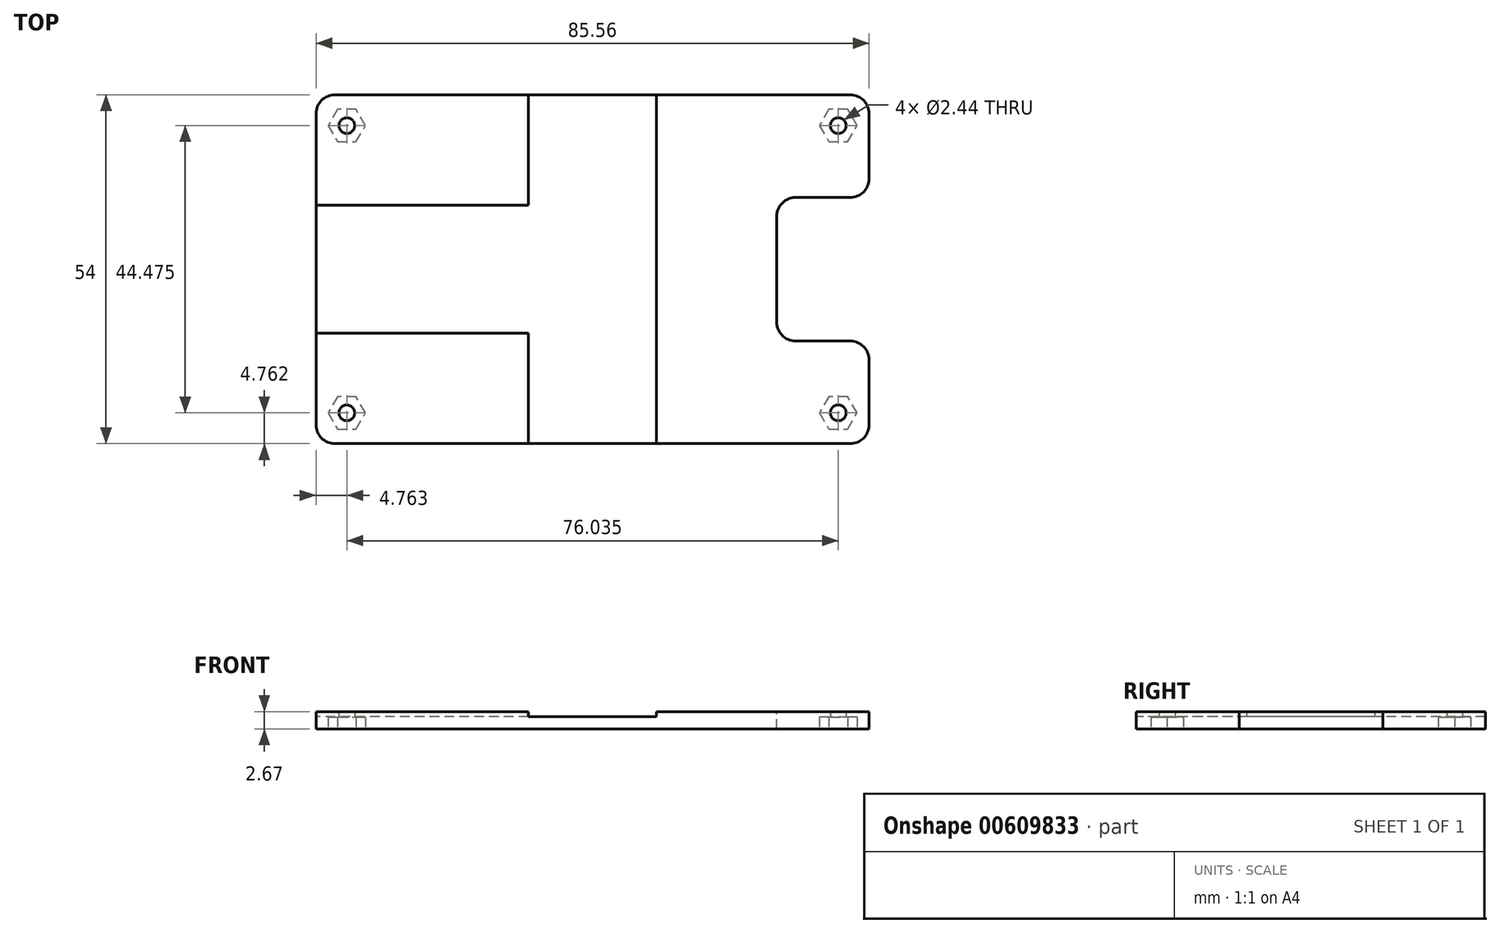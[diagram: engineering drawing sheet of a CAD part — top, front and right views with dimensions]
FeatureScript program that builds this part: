
annotation { "Feature Type Name" : "Feature", "Feature Type Description" : "" }
export const myFeature = defineFeature(function(context is Context, id is Id, definition is map)
    precondition{}
    {
        {
            var Q0;
            Q0=qCreatedBy(makeId("Top.planeOp"),FACE);
            var sketch = newSketch(context, id + "F0", { "sketchPlane" : qUnion([Q0])});
            skLineSegment(sketch, "E0.bottom", {"start": v(-39.86, 27) * mm, "end": v(39.86, 27) * mm});
            skLineSegment(sketch, "E0.top", {"start": v(-39.86, -27) * mm, "end": v(39.86, -27) * mm});
            skLineSegment(sketch, "E0.left", {"start": v(-42.78, 24.08) * mm, "end": v(-42.78, -24.08) * mm});
            skLineSegment(sketch, "E0.right", {"start": v(42.78, 24.08) * mm, "end": v(42.78, -24.08) * mm});
            skPoint(sketch, "E0.middle", {"position": v(0, 0) * mm});
            skPoint(sketch, "E1.visualSharp", {"position": v(-42.78, 27) * mm});
            skArc(sketch, "E1.filletArc", {"start": v(-39.86, 27) * mm, "mid": v(-41.92, 26.14) * mm, "end": v(-42.78, 24.08) * mm});
            skPoint(sketch, "E2.visualSharp", {"position": v(-42.78, -27) * mm});
            skArc(sketch, "E2.filletArc", {"start": v(-42.78, -24.08) * mm, "mid": v(-41.92, -26.14) * mm, "end": v(-39.86, -27) * mm});
            skPoint(sketch, "E3.visualSharp", {"position": v(42.78, -27) * mm});
            skArc(sketch, "E3.filletArc", {"start": v(39.86, -27) * mm, "mid": v(41.92, -26.14) * mm, "end": v(42.78, -24.08) * mm});
            skPoint(sketch, "E4.visualSharp", {"position": v(42.78, 27) * mm});
            skArc(sketch, "E4.filletArc", {"start": v(42.78, 24.08) * mm, "mid": v(41.92, 26.14) * mm, "end": v(39.86, 27) * mm});
            skSolve(sketch);
        }
        {
            var Q0;
            Q0 = qSketchRegion(id + "F0", true);
            extrude(context, id + "F1", {"entities" : qUnion([Q0]), "depth" : 2.67 * mm, "offsetDistance" : 25.4 * mm});
        }
        {
            var Q0;
            Q0=makeQuery(id+"F1.opExtrude","CAP_FACE",FACE,{"disambiguationData":[OSD([sQuery(id+"F0.wireOp",EDGE,"E0.bottom"),sQuery(id+"F0.wireOp",EDGE,"E0.top"),sQuery(id+"F0.wireOp",EDGE,"E0.left"),sQuery(id+"F0.wireOp",EDGE,"E0.right"),sQuery(id+"F0.wireOp",EDGE,"E1.filletArc"),sQuery(id+"F0.wireOp",EDGE,"E2.filletArc"),sQuery(id+"F0.wireOp",EDGE,"E3.filletArc"),sQuery(id+"F0.wireOp",EDGE,"E4.filletArc")])],"isStart":true});
            var sketch = newSketch(context, id + "F2", { "sketchPlane" : qUnion([Q0])});
            skLineSegment(sketch, "E5.bottom", {"start": v(-38.02, 22.24) * mm, "end": v(38.02, 22.24) * mm, "construction": true});
            skLineSegment(sketch, "E5.top", {"start": v(-38.02, -22.24) * mm, "end": v(38.02, -22.24) * mm, "construction": true});
            skLineSegment(sketch, "E5.left", {"start": v(-38.02, 22.24) * mm, "end": v(-38.02, -22.24) * mm, "construction": true});
            skLineSegment(sketch, "E5.right", {"start": v(38.02, 22.24) * mm, "end": v(38.02, -22.24) * mm, "construction": true});
            skPoint(sketch, "E5.middle", {"position": v(0, 0) * mm});
            skLineSegment(sketch, "E6", {"start": v(0, 22.24) * mm, "end": v(0, 27) * mm, "construction": true});
            skLineSegment(sketch, "E7", {"start": v(-38.02, 0) * mm, "end": v(-42.78, 0) * mm, "construction": true});
            skCircle(sketch, "E8", {"center": v(-38.02, 22.24) * mm, "radius": 1.22 * mm});
            skCircle(sketch, "E9", {"center": v(-38.02, -22.24) * mm, "radius": 1.22 * mm});
            skCircle(sketch, "E10", {"center": v(38.02, -22.24) * mm, "radius": 1.22 * mm});
            skCircle(sketch, "E11", {"center": v(38.02, 22.24) * mm, "radius": 1.22 * mm});
            skSolve(sketch);
        }
        {
            var Q0;
            Q0 = qSketchRegion(id + "F2", true);
            extrude(context, id + "F3", {"entities" : qUnion([Q0]), "operationType" : NewBodyOperationType.REMOVE, "endBound" : BoundingType.THROUGH_ALL, "oppositeDirection" : true, "depth" : 25.4 * mm, "offsetDistance" : 25.4 * mm});
        }
        {
            var Q0;
            Q0=makeQuery(id+"F1.opExtrude","CAP_FACE",FACE,{"disambiguationData":[OSD([sQuery(id+"F0.wireOp",EDGE,"E0.bottom"),sQuery(id+"F0.wireOp",EDGE,"E0.top"),sQuery(id+"F0.wireOp",EDGE,"E0.left"),sQuery(id+"F0.wireOp",EDGE,"E0.right"),sQuery(id+"F0.wireOp",EDGE,"E1.filletArc"),sQuery(id+"F0.wireOp",EDGE,"E2.filletArc"),sQuery(id+"F0.wireOp",EDGE,"E3.filletArc"),sQuery(id+"F0.wireOp",EDGE,"E4.filletArc")])],"isStart":true});
            var sketch = newSketch(context, id + "F4", { "sketchPlane" : qUnion([Q0])});
            skCircle(sketch, "E12.cCircle", {"center": v(-38.02, 22.24) * mm, "radius": 2.5 * mm, "construction": true});
            skLineSegment(sketch, "E12.0", {"start": v(-35.12, 22.24) * mm, "end": v(-36.57, 19.73) * mm});
            skLineSegment(sketch, "E12.1", {"start": v(-36.57, 19.73) * mm, "end": v(-39.47, 19.73) * mm});
            skLineSegment(sketch, "E12.2", {"start": v(-39.47, 19.73) * mm, "end": v(-40.91, 22.24) * mm});
            skLineSegment(sketch, "E12.3", {"start": v(-40.91, 22.24) * mm, "end": v(-39.47, 24.75) * mm});
            skLineSegment(sketch, "E12.4", {"start": v(-39.47, 24.75) * mm, "end": v(-36.57, 24.75) * mm});
            skLineSegment(sketch, "E12.5", {"start": v(-36.57, 24.75) * mm, "end": v(-35.12, 22.24) * mm});
            skPoint(sketch, "E12.0.midPoint", {"position": v(-35.85, 20.98) * mm});
            skCircle(sketch, "E13.cCircle", {"center": v(-38.02, -22.24) * mm, "radius": 2.5 * mm, "construction": true});
            skLineSegment(sketch, "E13.0", {"start": v(-36.57, -19.73) * mm, "end": v(-35.12, -22.24) * mm});
            skLineSegment(sketch, "E13.1", {"start": v(-35.12, -22.24) * mm, "end": v(-36.57, -24.75) * mm});
            skLineSegment(sketch, "E13.2", {"start": v(-36.57, -24.75) * mm, "end": v(-39.47, -24.75) * mm});
            skLineSegment(sketch, "E13.3", {"start": v(-39.47, -24.75) * mm, "end": v(-40.91, -22.24) * mm});
            skLineSegment(sketch, "E13.4", {"start": v(-40.91, -22.24) * mm, "end": v(-39.47, -19.73) * mm});
            skLineSegment(sketch, "E13.5", {"start": v(-39.47, -19.73) * mm, "end": v(-36.57, -19.73) * mm});
            skPoint(sketch, "E13.0.midPoint", {"position": v(-35.85, -20.98) * mm});
            skCircle(sketch, "E14.cCircle", {"center": v(38.02, 22.24) * mm, "radius": 2.5 * mm, "construction": true});
            skLineSegment(sketch, "E14.0", {"start": v(36.57, 19.73) * mm, "end": v(35.12, 22.24) * mm});
            skLineSegment(sketch, "E14.1", {"start": v(35.12, 22.24) * mm, "end": v(36.57, 24.75) * mm});
            skLineSegment(sketch, "E14.2", {"start": v(36.57, 24.75) * mm, "end": v(39.47, 24.75) * mm});
            skLineSegment(sketch, "E14.3", {"start": v(39.47, 24.75) * mm, "end": v(40.91, 22.24) * mm});
            skLineSegment(sketch, "E14.4", {"start": v(40.91, 22.24) * mm, "end": v(39.47, 19.73) * mm});
            skLineSegment(sketch, "E14.5", {"start": v(39.47, 19.73) * mm, "end": v(36.57, 19.73) * mm});
            skPoint(sketch, "E14.0.midPoint", {"position": v(35.85, 20.98) * mm});
            skCircle(sketch, "E15.cCircle", {"center": v(38.02, -22.24) * mm, "radius": 2.5 * mm, "construction": true});
            skLineSegment(sketch, "E15.0", {"start": v(35.12, -22.24) * mm, "end": v(36.57, -19.73) * mm});
            skLineSegment(sketch, "E15.1", {"start": v(36.57, -19.73) * mm, "end": v(39.47, -19.73) * mm});
            skLineSegment(sketch, "E15.2", {"start": v(39.47, -19.73) * mm, "end": v(40.91, -22.24) * mm});
            skLineSegment(sketch, "E15.3", {"start": v(40.91, -22.24) * mm, "end": v(39.47, -24.75) * mm});
            skLineSegment(sketch, "E15.4", {"start": v(39.47, -24.75) * mm, "end": v(36.57, -24.75) * mm});
            skLineSegment(sketch, "E15.5", {"start": v(36.57, -24.75) * mm, "end": v(35.12, -22.24) * mm});
            skPoint(sketch, "E15.0.midPoint", {"position": v(35.85, -20.98) * mm});
            skSolve(sketch);
        }
        {
            var Q0;
            Q0 = qSketchRegion(id + "F4", true);
            extrude(context, id + "F5", {"entities" : qUnion([Q0]), "operationType" : NewBodyOperationType.REMOVE, "oppositeDirection" : true, "depth" : 1.84 * mm, "offsetDistance" : 25.4 * mm});
        }
        {
            var Q0;
            Q0=makeQuery(id+"F1.opExtrude","CAP_FACE",FACE,{"disambiguationData":[OSD([sQuery(id+"F0.wireOp",EDGE,"E0.bottom"),sQuery(id+"F0.wireOp",EDGE,"E0.top"),sQuery(id+"F0.wireOp",EDGE,"E0.left"),sQuery(id+"F0.wireOp",EDGE,"E0.right"),sQuery(id+"F0.wireOp",EDGE,"E1.filletArc"),sQuery(id+"F0.wireOp",EDGE,"E2.filletArc"),sQuery(id+"F0.wireOp",EDGE,"E3.filletArc"),sQuery(id+"F0.wireOp",EDGE,"E4.filletArc")])],"isStart":false});
            var sketch = newSketch(context, id + "F6", { "sketchPlane" : qUnion([Q0])});
            skLineSegment(sketch, "E16", {"start": v(0, 27) * mm, "end": v(0, -27) * mm, "construction": true});
            skLineSegment(sketch, "E17", {"start": v(0, 0) * mm, "end": v(-42.78, 0) * mm, "construction": true});
            skLineSegment(sketch, "E18.0", {"start": v(-9.9, 27) * mm, "end": v(-9.9, 9.9) * mm});
            skLineSegment(sketch, "E19.0", {"start": v(9.9, 27) * mm, "end": v(9.9, -27) * mm});
            skLineSegment(sketch, "E20", {"start": v(-9.9, 27) * mm, "end": v(9.9, 27) * mm});
            skLineSegment(sketch, "E21", {"start": v(-9.9, -27) * mm, "end": v(9.9, -27) * mm});
            skLineSegment(sketch, "E22.0", {"start": v(-9.9, 9.9) * mm, "end": v(-42.78, 9.9) * mm});
            skLineSegment(sketch, "E23.0", {"start": v(-9.9, -9.9) * mm, "end": v(-42.78, -9.9) * mm});
            skLineSegment(sketch, "E24", {"start": v(-42.78, 9.9) * mm, "end": v(-42.78, -9.9) * mm});
            skLineSegment(sketch, "E25.trimOffspring", {"start": v(-9.9, -9.9) * mm, "end": v(-9.9, -27) * mm});
            skSolve(sketch);
        }
        {
            var Q0;
            Q0 = qSketchRegion(id + "F6", true);
            extrude(context, id + "F7", {"entities" : qUnion([Q0]), "operationType" : NewBodyOperationType.REMOVE, "oppositeDirection" : true, "depth" : 0.76 * mm, "offsetDistance" : 25.4 * mm});
        }
        {
            var Q0;
            {var subQ0=sQuery(id+"F0.wireOp",EDGE,"E3.filletArc");var subQ1=sQuery(id+"F0.wireOp",EDGE,"E0.top");var subQ2=sQuery(id+"F0.wireOp",EDGE,"E0.right");var subQ3=sQuery(id+"F0.wireOp",EDGE,"E0.bottom");var subQ4=sQuery(id+"F0.wireOp",EDGE,"E4.filletArc");Q0=makeQuery(id+"F7.boolean.opBoolean","SPLIT",FACE,{"disambiguationData":[TD([makeQuery(id+"F1.opExtrude","SWEPT_FACE",FACE,{"disambiguationData":[OSD([subQ2])]})])],"derivedFrom":makeQuery(id+"F1.opExtrude","CAP_FACE",FACE,{"disambiguationData":[OSD([subQ3,subQ1,sQuery(id+"F0.wireOp",EDGE,"E0.left"),subQ2,sQuery(id+"F0.wireOp",EDGE,"E1.filletArc"),sQuery(id+"F0.wireOp",EDGE,"E2.filletArc"),subQ0,subQ4])],"isStart":false})});}
            var sketch = newSketch(context, id + "F8", { "sketchPlane" : qUnion([Q0])});
            skLineSegment(sketch, "E26.bottom", {"start": v(31.41, 11.11) * mm, "end": v(57.07, 11.11) * mm});
            skLineSegment(sketch, "E26.top", {"start": v(31.41, -11.11) * mm, "end": v(57.07, -11.11) * mm});
            skLineSegment(sketch, "E26.left", {"start": v(28.5, 8.2) * mm, "end": v(28.5, -8.2) * mm});
            skLineSegment(sketch, "E26.right", {"start": v(57.07, 11.11) * mm, "end": v(57.07, -11.11) * mm});
            skPoint(sketch, "E26.middle", {"position": v(42.78, 0) * mm});
            skPoint(sketch, "E27.visualSharp", {"position": v(28.5, 11.11) * mm});
            skArc(sketch, "E27.filletArc", {"start": v(31.41, 11.11) * mm, "mid": v(29.35, 10.26) * mm, "end": v(28.5, 8.2) * mm});
            skPoint(sketch, "E28.visualSharp", {"position": v(28.5, -11.11) * mm});
            skArc(sketch, "E28.filletArc", {"start": v(28.5, -8.2) * mm, "mid": v(29.35, -10.26) * mm, "end": v(31.41, -11.11) * mm});
            skSolve(sketch);
        }
        {
            var Q0;
            Q0 = qSketchRegion(id + "F8", true);
            extrude(context, id + "F9", {"entities" : qUnion([Q0]), "operationType" : NewBodyOperationType.REMOVE, "endBound" : BoundingType.THROUGH_ALL, "oppositeDirection" : true, "depth" : 25.4 * mm, "offsetDistance" : 25.4 * mm});
        }
        {
            var Q0;
            Q0=makeQuery(id+"F9.boolean.opBoolean","INTERSECT",EDGE,{"derivedFrom":[makeQuery(id+"F1.opExtrude","SWEPT_FACE",FACE,{"disambiguationData":[OSD([sQuery(id+"F0.wireOp",EDGE,"E0.right")])]}),makeQuery(id+"F9.opExtrude","SWEPT_FACE",FACE,{"disambiguationData":[OSD([sQuery(id+"F8.wireOp",EDGE,"E26.bottom")])]})]});
            var Q1;
            Q1=makeQuery(id+"F9.boolean.opBoolean","INTERSECT",EDGE,{"derivedFrom":[makeQuery(id+"F1.opExtrude","SWEPT_FACE",FACE,{"disambiguationData":[OSD([sQuery(id+"F0.wireOp",EDGE,"E0.right")])]}),makeQuery(id+"F9.opExtrude","SWEPT_FACE",FACE,{"disambiguationData":[OSD([sQuery(id+"F8.wireOp",EDGE,"E26.top")])]})]});
            fillet(context, id + "F10", {"entities" : qUnion([Q0, Q1]), "radius" : 2.92 * mm, "tangentPropagation" : true, "allowEdgeOverflow" : false});
        }
    });
